FCSTD DOCUMENT  (FreeCAD 0.19R24366 (Git))
Label: assembly
License: All rights reserved
LicenseURL: http://en.wikipedia.org/wiki/All_rights_reserved
objects: App::DocumentObjectGroup×2, App::FeaturePython×2, PartDesign::CoordinateSystem×1, App::Link×1, App::Part×1
note: 1 computed .brp shape members not serialized (recipe doc carries the construction recipe); baked Part::Feature solids carry a one-line shape summary decoded from their .brp
EXTERNAL_REF file=vertical.FCStd obj=Part

FEATURE [App::DocumentObjectGroup] Parts
FEATURE [PartDesign::CoordinateSystem] LCS_Origin
  AttacherType = Attacher::AttachEngine3D
  MapMode = 2
  Support = -> [X_Axis]
FEATURE [App::DocumentObjectGroup] Constraints
FEATURE [App::FeaturePython] Variables  # WARN: FeaturePython — macro-defined, semantics opaque (R4)
FEATURE [App::FeaturePython] PropertyBag  label="Attributes"  # WARN: FeaturePython — macro-defined, semantics opaque (R4)
  CustomPropertyGroups = BaseProperties
  NrBoxesHor = 5
  NrBoxesVer = 1
FEATURE [App::Link] vertical_vertical
  AssemblyType = Asm4EE
  AttachedBy = #OriginVer
  AttachedTo = Parent Assembly#LCS_Origin
  LinkedObject = -> <external vertical.FCStd>#Part
FEATURE [App::Part] Model
  Configuration = 0
  Group = -> [LCS_Origin,Constraints,Variables,vertical_vertical]
  Origin = -> Origin
  Type = Assembly4 Model
